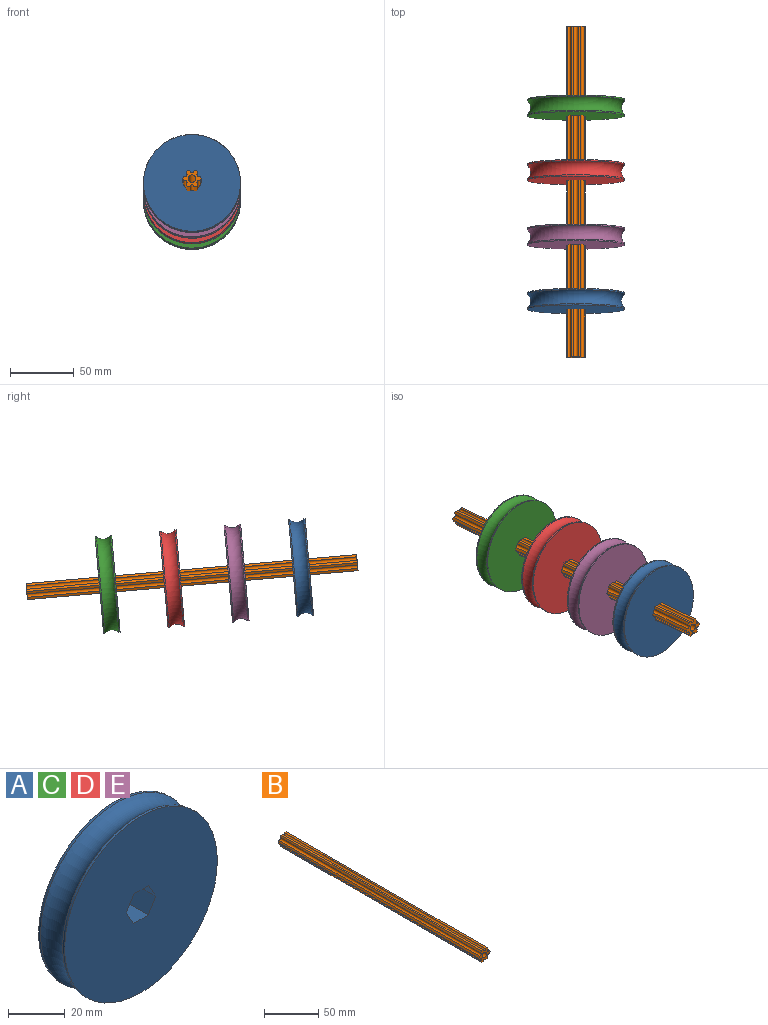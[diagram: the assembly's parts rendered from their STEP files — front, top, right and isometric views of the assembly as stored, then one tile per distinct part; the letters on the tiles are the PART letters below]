
ASSEMBLY  parts=5 mates=4
PART A: 11 faces, bbox 93.5x15x93.5 mm
  f0: cylinder r=38.1mm len=76.2mm, axis (0,-1,0), area 233.6mm2, adj f9,f10
  f1: cylinder r=38.1mm len=76.2mm, axis (0,-1,0), area 233.6mm2, adj f8,f10
  f2: plane 13x6.35mm, normal (0.87,0,-0.5), area 95.3mm2, adj f3,f7,f8,f9
  f3: plane 13x7.33mm, normal (0,0,-1), area 95.3mm2, adj f2,f4,f8,f9
  f4: plane 13x6.35mm, normal (-0.87,0,-0.5), area 95.3mm2, adj f3,f5,f8,f9
  f5: plane 13x6.35mm, normal (-0.87,0,0.5), area 95.3mm2, adj f4,f6,f8,f9
  f6: plane 13x7.33mm, normal (0,0,1), area 95.3mm2, adj f5,f7,f8,f9
  f7: plane 13x6.35mm, normal (0.87,0,0.5), area 95.3mm2, adj f2,f6,f8,f9
  f8: plane 76.2x76.2mm, normal (0,1,0), area 4420.7mm2, adj f1,f2,f3,f4,f5,f6,f7
  f9: plane 76.2x76.2mm, normal (0,-1,0), area 4420.7mm2, adj f0,f2,f3,f4,f5,f6,f7
  f10: torus R=43.18mm, axis (0,1,0), area 2847.8mm2, adj f0,f1
PART B: 21 faces, bbox 14.7x260.5x12.7 mm
  f0: plane 14.66x12.7mm, normal (0,-1,0), area 88.9mm2, adj f1,f2,f3,f4,f5,f6,f7,f8
  f1: plane 260.46x1.8mm, normal (0.87,0,-0.5), area 541.4mm2, adj f0,f2,f18,f20
  f2: plane 260.46x1.8mm, normal (0.87,0,0.5), area 541.4mm2, adj f0,f1,f3,f20
  f3: cylinder r=1.59mm len=260.46mm, axis (0,1,0), area 1299mm2, adj f0,f2,f4,f20
  f4: plane 260.46x1.8mm, normal (0.87,0,0.5), area 541.4mm2, adj f0,f3,f5,f20
  f5: plane 260.46x2.08mm, normal (0,0,1), area 541.4mm2, adj f0,f4,f6,f20
  f6: cylinder r=1.59mm len=260.46mm, axis (0,1,0), area 1299mm2, adj f0,f5,f7,f20
  f7: plane 260.46x2.08mm, normal (0,0,1), area 541.4mm2, adj f0,f6,f8,f20
  f8: plane 260.46x1.8mm, normal (-0.87,0,0.5), area 541.4mm2, adj f0,f7,f9,f20
  f9: cylinder r=1.59mm len=260.46mm, axis (0,1,0), area 1299mm2, adj f0,f8,f10,f20
  f10: plane 260.46x1.8mm, normal (-0.87,0,0.5), area 541.4mm2, adj f0,f9,f11,f20
  f11: plane 260.46x1.8mm, normal (-0.87,0,-0.5), area 541.4mm2, adj f0,f10,f12,f20
  f12: cylinder r=1.59mm len=260.46mm, axis (0,1,0), area 1299mm2, adj f0,f11,f13,f20
  f13: plane 260.46x1.8mm, normal (-0.87,0,-0.5), area 541.4mm2, adj f0,f12,f14,f20
  f14: plane 260.46x2.08mm, normal (0,0,-1), area 541.4mm2, adj f0,f13,f15,f20
  f15: cylinder r=1.59mm len=260.46mm, axis (0,1,0), area 1299mm2, adj f0,f14,f16,f20
  f16: plane 260.46x2.08mm, normal (0,0,-1), area 541.4mm2, adj f0,f15,f17,f20
  f17: plane 260.46x1.8mm, normal (0.87,0,-0.5), area 541.4mm2, adj f0,f16,f18,f20
  f18: cylinder r=1.59mm len=260.46mm, axis (0,1,0), area 1299mm2, adj f0,f1,f17,f20
  f19: cylinder r=2.93mm len=260.46mm, axis (0,1,0), area 4801mm2, adj f0,f20
  f20: plane 14.66x12.7mm, normal (0,1,0), area 88.9mm2, adj f1,f2,f3,f4,f5,f6,f7,f8
PART C: same geometry as A
PART D: same geometry as A
PART E: same geometry as A
PLACE A rot(axis=(1,0,0),175deg) t=(376.78,-167.63,189.96)mm
PLACE B rot(axis=(-1,0,0),5deg) t=(376.78,-47.44,179.44)mm
PLACE C rot(axis=(1,0,0),175deg) t=(376.78,-15.81,176.67)mm
PLACE D rot(axis=(-1,0,0),5deg) t=(376.78,91.43,167.29)mm
PLACE E rot(axis=(1,0,0),175deg) t=(376.78,-117.02,185.53)mm
MATE slider A.f0 <-> B.f19  axis (0,1,-0.09) through (376.78,-82.23,182.48)mm
MATE slider E.f0 <-> B.f19  axis (0,1,-0.09) through (376.78,-31.62,178.06)mm
MATE slider D.f0 <-> B.f19  axis (0,1,-0.09) through (376.78,18.99,173.63)mm
MATE slider C.f0 <-> B.f19  axis (0,1,-0.09) through (376.78,69.59,169.2)mm
